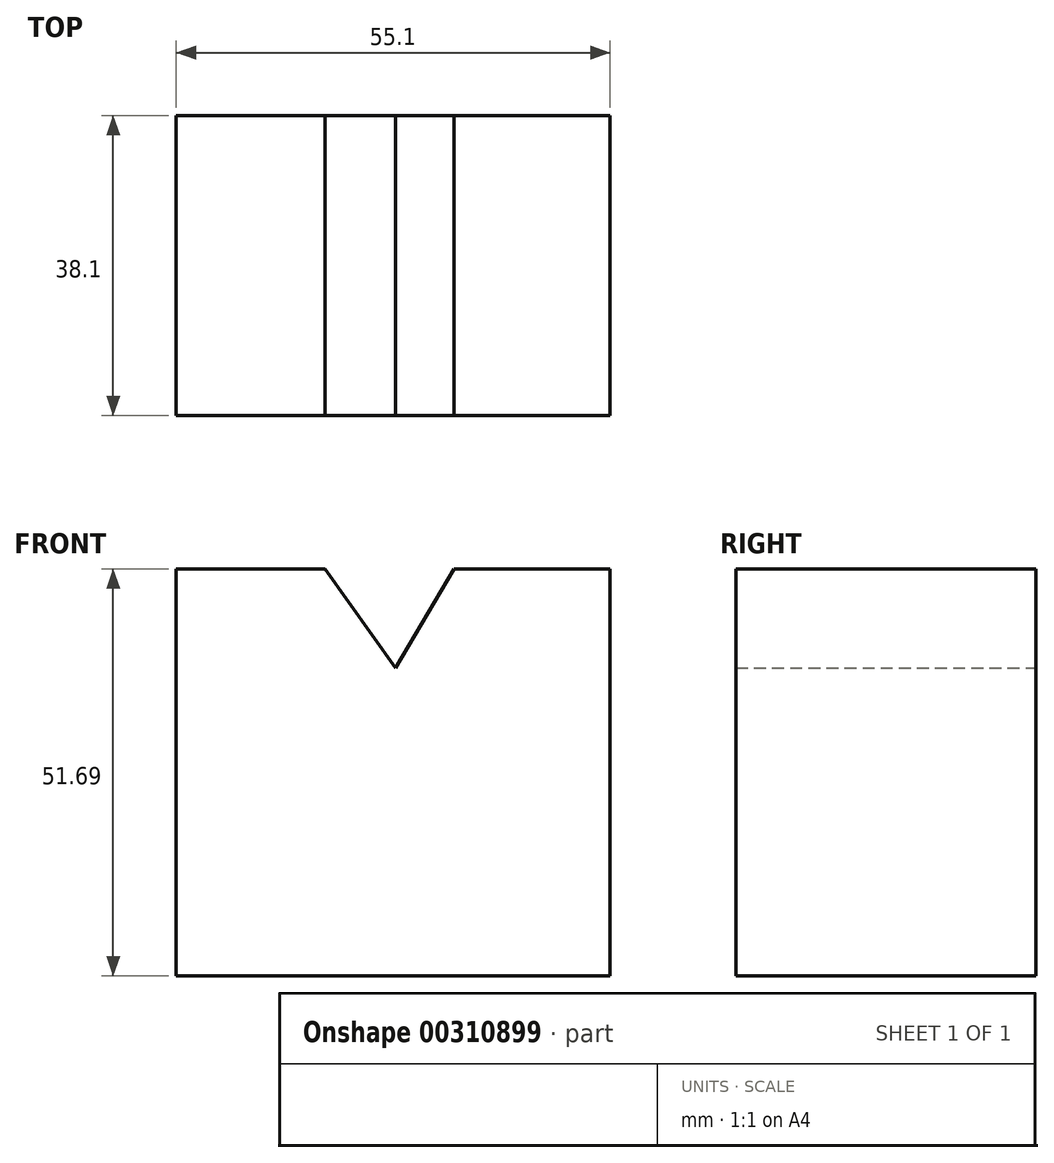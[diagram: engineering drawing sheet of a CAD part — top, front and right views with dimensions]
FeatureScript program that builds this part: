
annotation { "Feature Type Name" : "Feature", "Feature Type Description" : "" }
export const myFeature = defineFeature(function(context is Context, id is Id, definition is map)
    precondition{}
    {
        {
            var Q0;
            Q0=qCreatedBy(makeId("Front.planeOp"),FACE);
            var sketch = newSketch(context, id + "F0", { "sketchPlane" : qUnion([Q0])});
            skLineSegment(sketch, "E0", {"start": v(-40.24, -39.15) * mm, "end": v(14.86, -39.15) * mm});
            skLineSegment(sketch, "E1", {"start": v(14.86, -39.15) * mm, "end": v(14.86, 12.54) * mm});
            skLineSegment(sketch, "E2", {"start": v(14.86, 12.54) * mm, "end": v(-4.95, 12.54) * mm});
            skLineSegment(sketch, "E3", {"start": v(-4.95, 12.54) * mm, "end": v(-12.38, 0) * mm});
            skLineSegment(sketch, "E4", {"start": v(-12.38, 0) * mm, "end": v(-21.36, 12.54) * mm});
            skLineSegment(sketch, "E5", {"start": v(-21.36, 12.54) * mm, "end": v(-40.24, 12.54) * mm});
            skLineSegment(sketch, "E6", {"start": v(-40.24, 12.54) * mm, "end": v(-40.24, -39.15) * mm});
            skSolve(sketch);
        }
        {
            var Q0;
            Q0=makeQuery(id+"F0.imprint","IMPRINT",FACE,{"disambiguationData":[TD([[makeQuery(id+"F0.imprint","IMPRINT",EDGE,{"derivedFrom":sQuery(id+"F0.wireOp",EDGE,"E0")}),1.0]])]});
            extrude(context, id + "F1", {"entities" : qUnion([Q0]), "depth" : 38.1 * mm});
        }
    });
